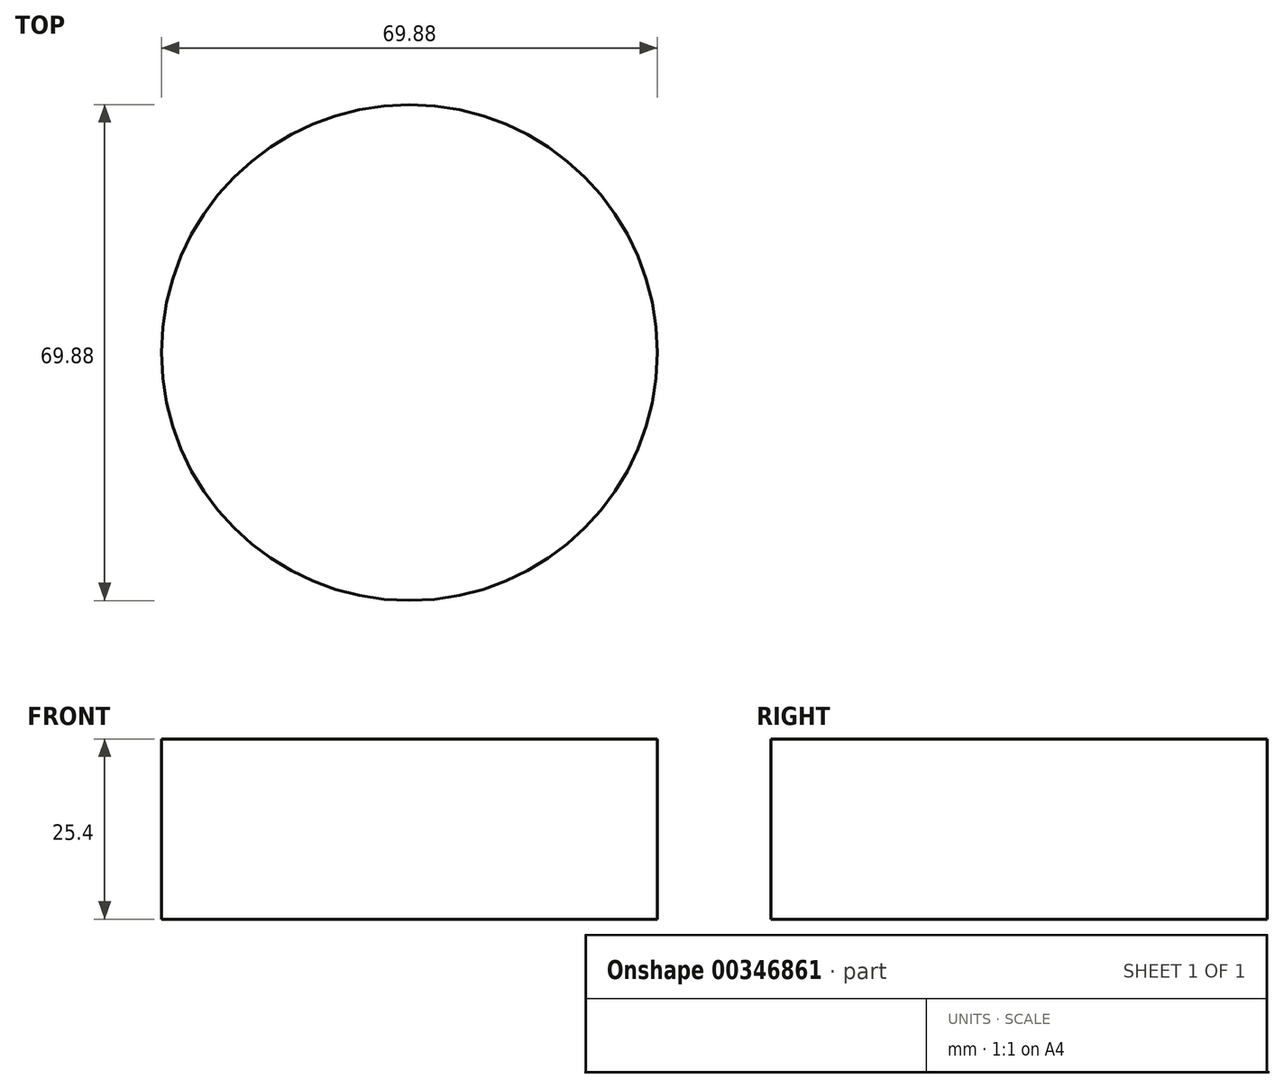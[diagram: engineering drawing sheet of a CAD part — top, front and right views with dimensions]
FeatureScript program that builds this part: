
annotation { "Feature Type Name" : "Feature", "Feature Type Description" : "" }
export const myFeature = defineFeature(function(context is Context, id is Id, definition is map)
    precondition{}
    {
        {
            var Q0;
            Q0=qCreatedBy(makeId("Top.planeOp"),FACE);
            var sketch = newSketch(context, id + "F0", { "sketchPlane" : qUnion([Q0])});
            skCircle(sketch, "E0", {"center": v(0, 0) * mm, "radius": 53.57 * mm});
            skCircle(sketch, "E1", {"center": v(0, 0) * mm, "radius": 34.94 * mm});
            skSolve(sketch);
        }
        {
            var Q0;
            Q0=makeQuery(id+"F0.imprint","IMPRINT",FACE,{"disambiguationData":[TD([[makeQuery(id+"F0.imprint","IMPRINT",EDGE,{"derivedFrom":sQuery(id+"F0.wireOp",EDGE,"E1")}),1.0]])]});
            extrude(context, id + "F1", {"entities" : qUnion([Q0]), "depth" : 25.4 * mm});
        }
    });
